# Revit family: ICF_Eng
name_source: partatom
category: Оборудование
units: mm (PartAtom-declared; Revit-internal decimal feet)

## family parameters
Всегда вертикально = Да
Классификация = Нет
На основе рабочей плоскости = Нет
Общий = Нет
При загрузке вырезать с полостями = Нет
Размер круглого соединителя = Использовать диаметр
Тип детали = Нормальный
Точка принадлежности помещению = Нет

## types (24) — shared parameters
00_20_Manufacturer = Vents
00_20_Name = Induction centrifugal fan
Casing Material = Steel, galvanized
Frequency = 50 Гц
Load Classification = HVAC
Maintenance zone material = <По категории>
Number of Fase = 3
Thrust = 0.00 Н
URL = https://ventilation-system.com
Voltage = 400 В
Изготовитель = Vents
zero-valued in all types: Width

## per-type parameters (varying)
| type | A | A1 | A2 | B | C | Height | L | L1 | Length | Maximum Air Flow | Mesh | Motor | Power | Weight | a | a1 | c1 | Отметка по умолчанию |
| ICF-50N-4 | 290 мм | 190 мм | 90 мм | 1355 мм | 935 мм | 290 мм | 180 мм | 410 мм | 1355 мм | 6200.0 м³/ч | Round mesh : 50N | Motor : Motor_1.5 кВт | 1500 Вт | 96.00 кг | 43 мм | 24 мм | 219 мм | 935 мм |
| ICF-100N-4 | 330 мм | 230 мм | 130 мм | 1605 мм | 1105 мм | 330 мм | 230 мм | 510 мм | 1605 мм | 10200.0 м³/ч | Round mesh : 100N | Motor : Motor_3 кВт | 3000 Вт | 138.00 кг | 63 мм | 37 мм | 261 мм | 1105 мм |
| ICF-85N-4 | 330 мм | 230 мм | 130 мм | 1605 мм | 1105 мм | 330 мм | 230 мм | 510 мм | 1605 мм | 9750.0 м³/ч | Round mesh : 85N | Motor : Motor_2.2 кВт | 2200 Вт | 136.00 кг | 63 мм | 37 мм | 261 мм | 1105 мм |
| ICF-50N-4-300/2 | 290 мм | 190 мм | 90 мм | 1355 мм | 935 мм | 290 мм | 180 мм | 410 мм | 1355 мм | 6200.0 м³/ч | Round mesh : 50N | Motor : Motor_1.5 кВт | 1500 Вт | 96.00 кг | 43 мм | 24 мм | 219 мм | 935 мм |
| ICF-50N-4-400/2 | 290 мм | 190 мм | 90 мм | 1355 мм | 935 мм | 290 мм | 180 мм | 410 мм | 1355 мм | 6200.0 м³/ч | Round mesh : 50N | Motor : Motor_1.5 кВт | 1500 Вт | 96.00 кг | 43 мм | 24 мм | 219 мм | 935 мм |
| ICF-50N-4/6 | 290 мм | 190 мм | 90 мм | 1355 мм | 935 мм | 290 мм | 180 мм | 410 мм | 1355 мм | 6200.0 м³/ч | Round mesh : 50N | Motor : Motor_1.5 кВт | 1500 Вт | 96.00 кг | 43 мм | 24 мм | 219 мм | 935 мм |
| ICF-50N-4/6-300/2 | 290 мм | 190 мм | 90 мм | 1355 мм | 935 мм | 290 мм | 180 мм | 410 мм | 1355 мм | 6200.0 м³/ч | Round mesh : 50N | Motor : Motor_1.5 кВт | 1500 Вт | 96.00 кг | 43 мм | 24 мм | 219 мм | 935 мм |
| ICF-50N-4/6-400/2 | 290 мм | 190 мм | 90 мм | 1355 мм | 935 мм | 290 мм | 180 мм | 410 мм | 1355 мм | 6200.0 м³/ч | Round mesh : 50N | Motor : Motor_1.5 кВт | 1500 Вт | 96.00 кг | 43 мм | 24 мм | 219 мм | 935 мм |
| ICF-50N-4/8 | 290 мм | 190 мм | 90 мм | 1355 мм | 935 мм | 290 мм | 180 мм | 410 мм | 1355 мм | 6200.0 м³/ч | Round mesh : 50N | Motor : Motor_1.6 кВт | 1600 Вт | 96.00 кг | 43 мм | 24 мм | 219 мм | 935 мм |
| ICF-50N-4/8-300/2 | 290 мм | 190 мм | 90 мм | 1355 мм | 935 мм | 290 мм | 180 мм | 410 мм | 1355 мм | 6200.0 м³/ч | Round mesh : 50N | Motor : Motor_1.6 кВт | 1600 Вт | 96.00 кг | 43 мм | 24 мм | 219 мм | 935 мм |
| ICF-50N-4/8-400/2 | 290 мм | 190 мм | 90 мм | 1355 мм | 935 мм | 290 мм | 180 мм | 410 мм | 1355 мм | 6200.0 м³/ч | Round mesh : 50N | Motor : Motor_1.6 кВт | 1600 Вт | 96.00 кг | 43 мм | 24 мм | 219 мм | 935 мм |
| ICF-85N-4-300/2 | 330 мм | 230 мм | 130 мм | 1605 мм | 1105 мм | 330 мм | 230 мм | 510 мм | 1605 мм | 9750.0 м³/ч | Round mesh : 85N | Motor : Motor_2.2 кВт | 2200 Вт | 136.00 кг | 63 мм | 37 мм | 261 мм | 1105 мм |
| ICF-85N-4-400/2 | 330 мм | 230 мм | 130 мм | 1605 мм | 1105 мм | 330 мм | 230 мм | 510 мм | 1605 мм | 9750.0 м³/ч | Round mesh : 85N | Motor : Motor_2.2 кВт | 2200 Вт | 136.00 кг | 63 мм | 37 мм | 261 мм | 1105 мм |
| ICF-85N-4/6 | 330 мм | 230 мм | 130 мм | 1605 мм | 1105 мм | 330 мм | 230 мм | 510 мм | 1605 мм | 9750.0 м³/ч | Round mesh : 85N | Motor : Motor_2.2 кВт | 2200 Вт | 136.00 кг | 63 мм | 37 мм | 261 мм | 1105 мм |
| ICF-85N-4/6-300/2 | 330 мм | 230 мм | 130 мм | 1605 мм | 1105 мм | 330 мм | 230 мм | 510 мм | 1605 мм | 9750.0 м³/ч | Round mesh : 85N | Motor : Motor_2.2 кВт | 2200 Вт | 136.00 кг | 63 мм | 37 мм | 261 мм | 1105 мм |
| ICF-85N-4/6-400/2 | 330 мм | 230 мм | 130 мм | 1605 мм | 1105 мм | 330 мм | 230 мм | 510 мм | 1605 мм | 9750.0 м³/ч | Round mesh : 85N | Motor : Motor_2.2 кВт | 2200 Вт | 136.00 кг | 63 мм | 37 мм | 261 мм | 1105 мм |
| ICF-85N-4/8 | 330 мм | 230 мм | 130 мм | 1605 мм | 1105 мм | 330 мм | 230 мм | 510 мм | 1605 мм | 9750.0 м³/ч | Round mesh : 85N | Motor : Motor_2.2 кВт | 2200 Вт | 136.00 кг | 63 мм | 37 мм | 261 мм | 1105 мм |
| ICF-85N-4/8-300/2 | 330 мм | 230 мм | 130 мм | 1605 мм | 1105 мм | 330 мм | 230 мм | 510 мм | 1605 мм | 9750.0 м³/ч | Round mesh : 85N | Motor : Motor_2.2 кВт | 2200 Вт | 136.00 кг | 63 мм | 37 мм | 261 мм | 1105 мм |
| ICF-85N-4/8-400/2 | 330 мм | 230 мм | 130 мм | 1605 мм | 1105 мм | 330 мм | 230 мм | 510 мм | 1605 мм | 9750.0 м³/ч | Round mesh : 85N | Motor : Motor_2.2 кВт | 2200 Вт | 136.00 кг | 63 мм | 37 мм | 261 мм | 1105 мм |
| ICF-100N-4-300/2 | 330 мм | 230 мм | 130 мм | 1605 мм | 1105 мм | 330 мм | 230 мм | 510 мм | 1605 мм | 10200.0 м³/ч | Round mesh : 100N | Motor : Motor_3 кВт | 3000 Вт | 138.00 кг | 63 мм | 37 мм | 261 мм | 1105 мм |
| ICF-100N-4-400/2 | 330 мм | 230 мм | 130 мм | 1605 мм | 1105 мм | 330 мм | 230 мм | 510 мм | 1605 мм | 10200.0 м³/ч | Round mesh : 100N | Motor : Motor_3 кВт | 3000 Вт | 138.00 кг | 63 мм | 37 мм | 261 мм | 1105 мм |
| ICF-100N-4/8 | 330 мм | 230 мм | 130 мм | 1605 мм | 1105 мм | 330 мм | 230 мм | 510 мм | 1605 мм | 10200.0 м³/ч | Round mesh : 100N | Motor : Motor_3 кВт | 3000 Вт | 138.00 кг | 63 мм | 37 мм | 261 мм | 1105 мм |
| ICF-100N-4/8-300/2 | 330 мм | 230 мм | 130 мм | 1605 мм | 1105 мм | 330 мм | 230 мм | 510 мм | 1605 мм | 10200.0 м³/ч | Round mesh : 100N | Motor : Motor_3 кВт | 3000 Вт | 138.00 кг | 63 мм | 37 мм | 261 мм | 1105 мм |
| ICF-100N-4/8-400/2 | 330 мм | 230 мм | 130 мм | 1605 мм | 1105 мм | 330 мм | 230 мм | 510 мм | 1605 мм | 10200.0 м³/ч | Round mesh : 100N | Motor : Motor_3 кВт | 3000 Вт | 138.00 кг | 63 мм | 37 мм | 261 мм | 1105 мм |

note: column(s) folded — value = type name in every type: 00_20_Type
